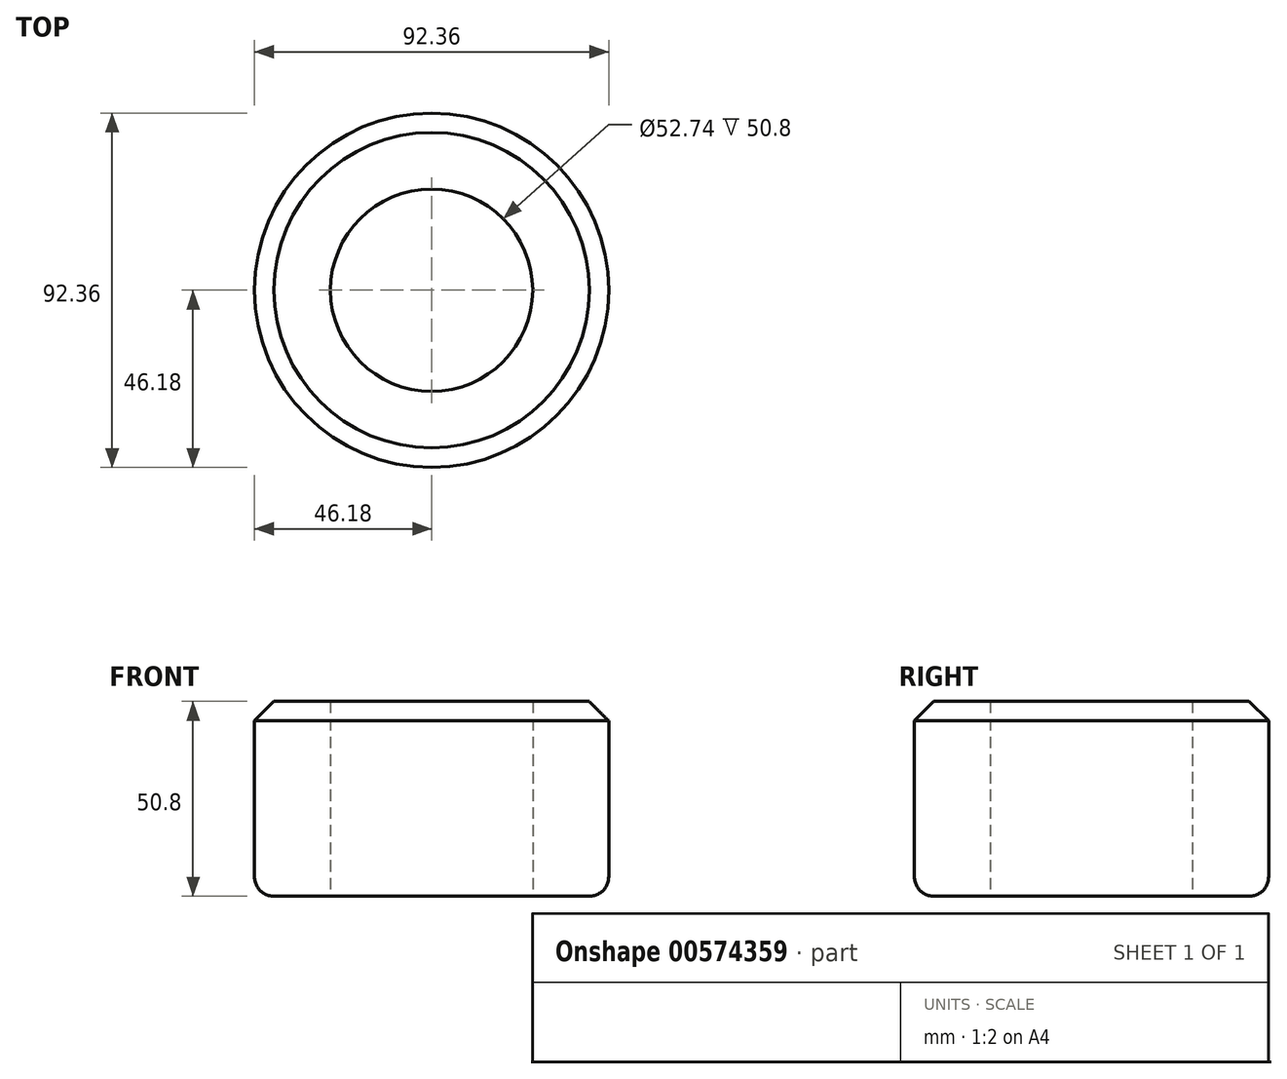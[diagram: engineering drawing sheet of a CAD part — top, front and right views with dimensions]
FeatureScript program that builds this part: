
annotation { "Feature Type Name" : "Feature", "Feature Type Description" : "" }
export const myFeature = defineFeature(function(context is Context, id is Id, definition is map)
    precondition{}
    {
        {
            var Q0;
            Q0=qCreatedBy(makeId("Top.planeOp"),FACE);
            var sketch = newSketch(context, id + "F0", { "sketchPlane" : qUnion([Q0])});
            skCircle(sketch, "E0", {"center": v(0, 0) * mm, "radius": 46.18 * mm});
            skCircle(sketch, "E1", {"center": v(0, 0) * mm, "radius": 26.37 * mm});
            skSolve(sketch);
        }
        {
            var Q0;
            Q0 = qSketchRegion(id + "F0", true);
            var Q1;
            Q1=makeQuery(id+"F0.imprint","IMPRINT",FACE,{"disambiguationData":[TD([[makeQuery(id+"F0.imprint","IMPRINT",EDGE,{"derivedFrom":sQuery(id+"F0.wireOp",EDGE,"E0")}),1.0]])]});
            extrude(context, id + "F1", {"entities" : qUnion([Q0, Q1]), "depth" : 50.8 * mm, "offsetDistance" : 25.4 * mm});
        }
        {
            var Q0;
            Q0=makeQuery(id+"F1.opExtrude","CAP_EDGE",EDGE,{"disambiguationData":[OSD([sQuery(id+"F0.wireOp",EDGE,"E0")])],"isStart":false});
            chamfer(context, id + "F2", {"entities" : qUnion([Q0]), "width" : 5.08 * mm, "tangentPropagation" : true});
        }
        {
            var Q0;
            Q0=makeQuery(id+"F1.opExtrude","CAP_EDGE",EDGE,{"disambiguationData":[OSD([sQuery(id+"F0.wireOp",EDGE,"E0")])],"isStart":true});
            fillet(context, id + "F3", {"entities" : qUnion([Q0]), "radius" : 5.08 * mm, "tangentPropagation" : true, "allowEdgeOverflow" : false});
        }
    });
